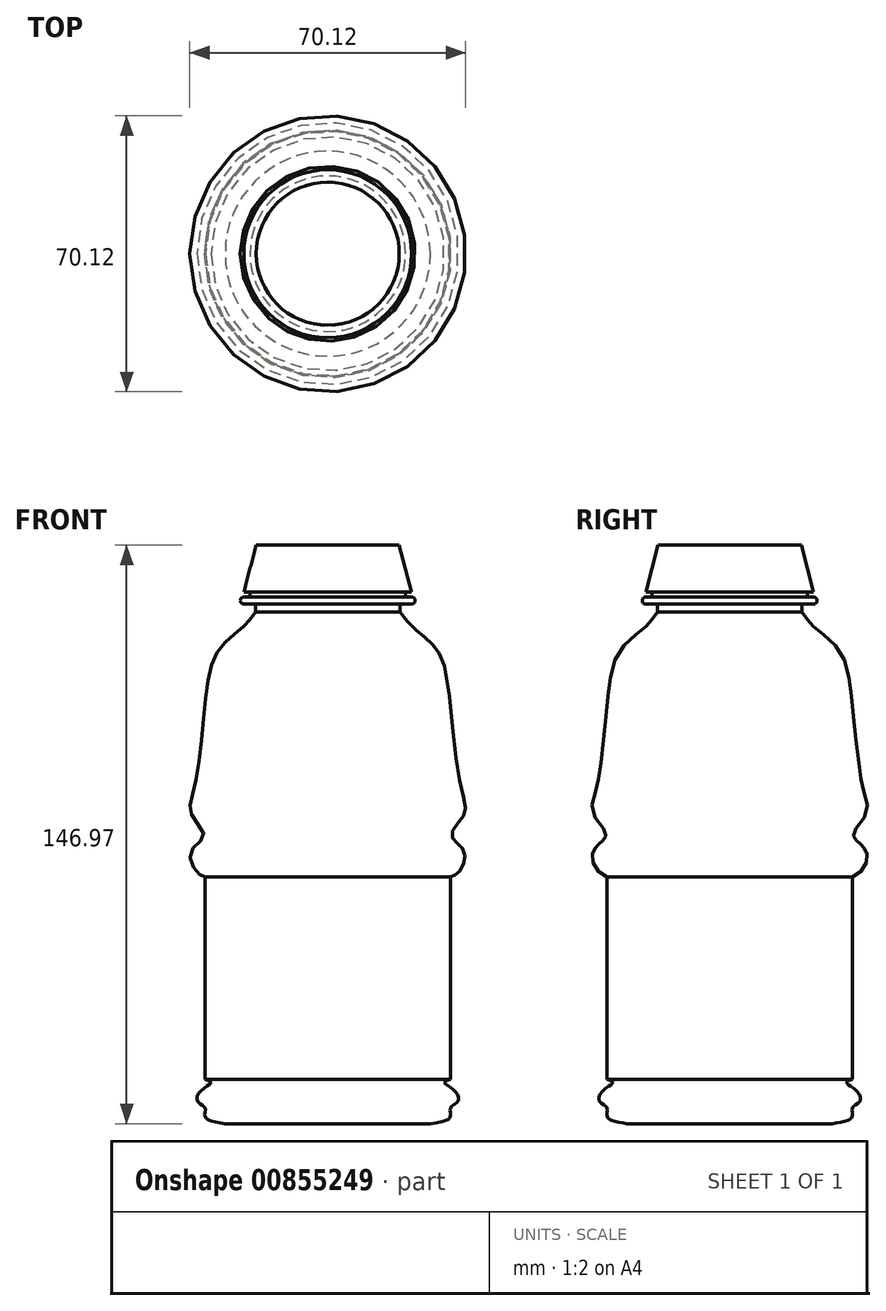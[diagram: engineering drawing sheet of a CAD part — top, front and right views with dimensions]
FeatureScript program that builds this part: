
annotation { "Feature Type Name" : "Feature", "Feature Type Description" : "" }
export const myFeature = defineFeature(function(context is Context, id is Id, definition is map)
    precondition{}
    {
        {
            var Q0;
            Q0=qCreatedBy(makeId("Front.planeOp"),FACE);
            var sketch = newSketch(context, id + "F0", { "sketchPlane" : qUnion([Q0])});
            skLineSegment(sketch, "E0", {"start": v(0, 0) * mm, "end": v(0, 146.97) * mm});
            skLineSegment(sketch, "E1", {"start": v(0, 146.97) * mm, "end": v(18.17, 146.97) * mm});
            skLineSegment(sketch, "E2", {"start": v(18.17, 146.97) * mm, "end": v(21.33, 135.12) * mm});
            skLineSegment(sketch, "E3", {"start": v(21.33, 135.12) * mm, "end": v(19.76, 135.12) * mm});
            skLineSegment(sketch, "E4", {"start": v(19.76, 135.12) * mm, "end": v(19.76, 133.8) * mm});
            skLineSegment(sketch, "E5", {"start": v(19.76, 133.8) * mm, "end": v(21.33, 133.8) * mm});
            skArc(sketch, "E6", {"start": v(21.33, 132.03) * mm, "mid": v(22.22, 132.92) * mm, "end": v(21.33, 133.8) * mm});
            skLineSegment(sketch, "E7", {"start": v(21.33, 132.03) * mm, "end": v(18.33, 132.03) * mm});
            skLineSegment(sketch, "E8", {"start": v(18.33, 132.03) * mm, "end": v(18.33, 130.05) * mm});
            skFitSpline(sketch, "E9", {"points": [v(18.33, 130.05) * mm, v(21.68, 126.04) * mm, v(27.8, 120.3) * mm, v(31.16, 106.88) * mm, v(33.92, 85.16) * mm, v(34.71, 78.64) * mm, v(31.46, 73.25) * mm, v(34.71, 69.16) * mm, v(33.33, 64.03) * mm, v(31.16, 62.65) * mm], "startDerivative": vector(31.94, -45.23) * mm, "endDerivative": vector(-33.35, -14.15) * mm});
            skLineSegment(sketch, "E10", {"start": v(31.16, 62.65) * mm, "end": v(31.16, 11.3) * mm});
            skFitSpline(sketch, "E11", {"points": [v(31.16, 11.3) * mm, v(29.7, 10.4) * mm, v(32.16, 8.41) * mm, v(33.1, 5.71) * mm, v(31.16, 3.95) * mm, v(31.16, 1.72) * mm, v(26.05, 0) * mm], "startDerivative": vector(-17.47, -6.3) * mm, "endDerivative": vector(-30.97, -4.63) * mm});
            skLineSegment(sketch, "E12", {"start": v(26.05, 0) * mm, "end": v(0, 0) * mm});
            skSolve(sketch);
        }
        {
            var Q0;
            Q0 = qSketchRegion(id + "F0", true);
            var Q1;
            Q1=sQuery(id+"F0.wireOp",EDGE,"E0");
            revolve(context, id + "F1", {"surfaceOperationType" : NewSurfaceOperationType.NEW, "entities" : qUnion([Q0]), "axis" : qUnion([Q1]), "revolveType" : RevolveType.FULL});
        }
    });
